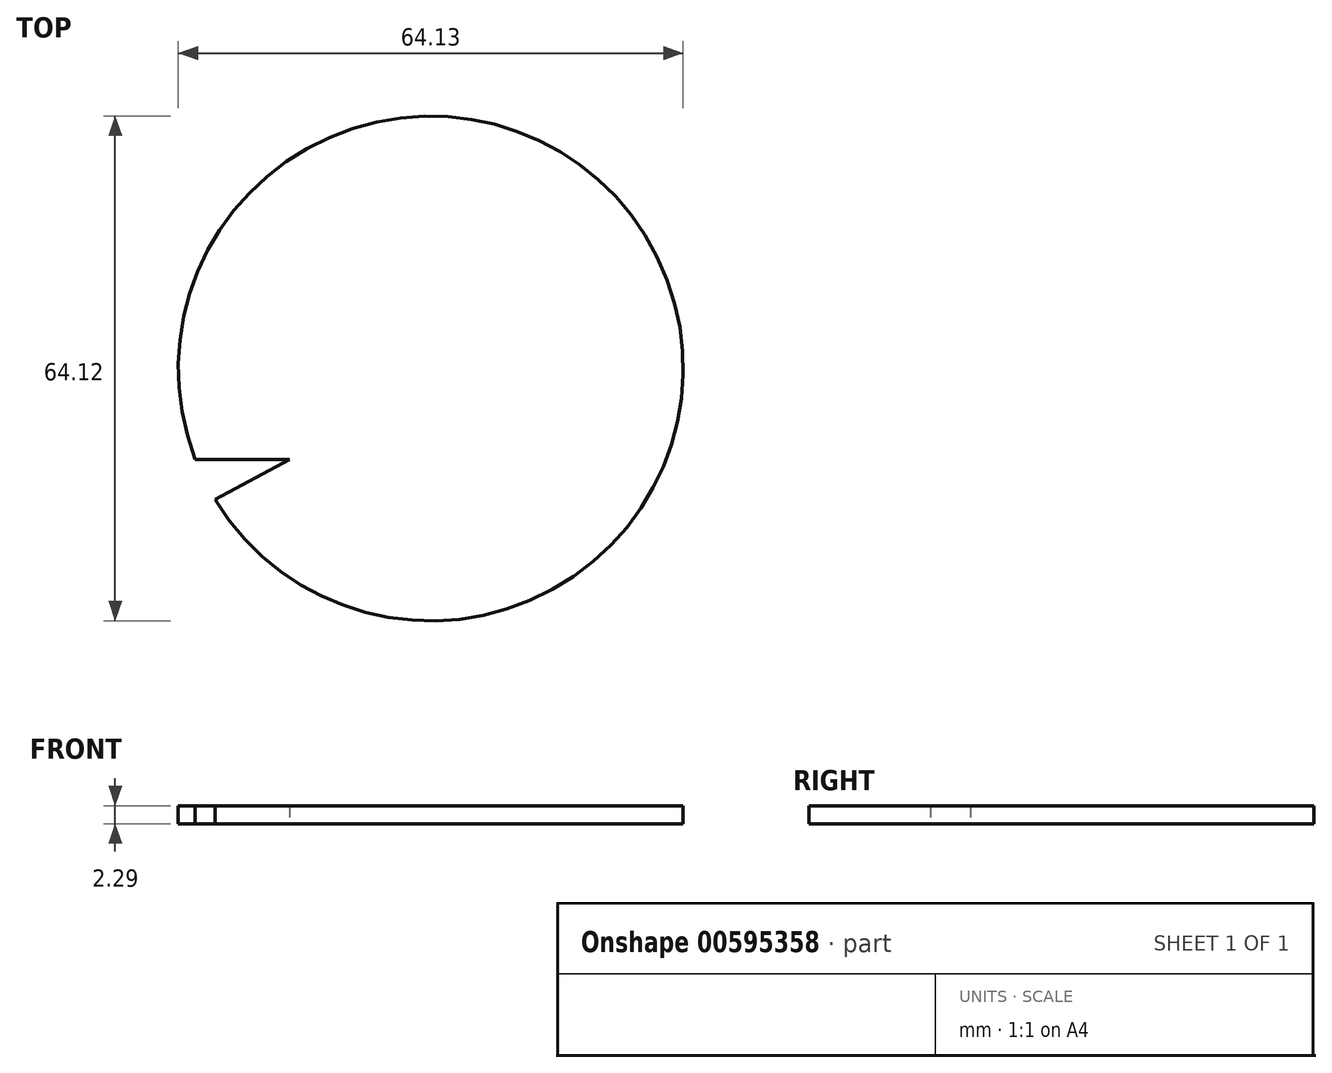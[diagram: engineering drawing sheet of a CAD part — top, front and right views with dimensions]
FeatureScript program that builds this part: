
annotation { "Feature Type Name" : "Feature", "Feature Type Description" : "" }
export const myFeature = defineFeature(function(context is Context, id is Id, definition is map)
    precondition{}
    {
        {
            var Q0;
            Q0=qCreatedBy(makeId("Top.planeOp"),FACE);
            var sketch = newSketch(context, id + "F0", { "sketchPlane" : qUnion([Q0])});
            skArc(sketch, "E0", {"start": v(-143.73, 0) * mm, "mid": v(-87.59, 30.84) * mm, "end": v(-146.25, 5.1) * mm});
            skLineSegment(sketch, "E1", {"start": v(-146.25, 5.1) * mm, "end": v(-134.24, 5.1) * mm});
            skLineSegment(sketch, "E2", {"start": v(-134.24, 5.1) * mm, "end": v(-143.73, 0) * mm});
            skLineSegment(sketch, "E3", {"start": v(-143.73, 0) * mm, "end": v(-143.73, 0) * mm});
            skSolve(sketch);
        }
        {
            var Q0;
            Q0 = qSketchRegion(id + "F0", true);
            extrude(context, id + "F1", {"entities" : qUnion([Q0]), "depth" : 2.3 * mm, "offsetDistance" : 25.4 * mm});
        }
        {
            var Q0;
            Q0 = qSketchRegion(id + "F0", true);
            extrude(context, id + "F2", {"entities" : qUnion([Q0]), "operationType" : NewBodyOperationType.ADD, "depth" : 2.3 * mm, "offsetDistance" : 25.4 * mm});
        }
    });
